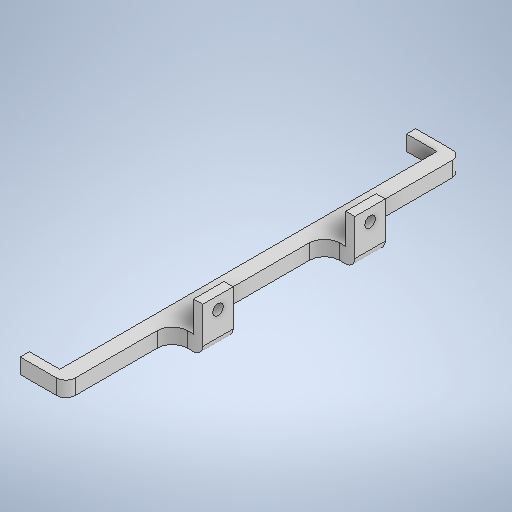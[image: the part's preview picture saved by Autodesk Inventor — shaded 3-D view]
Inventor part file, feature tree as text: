
AUTODESK INVENTOR PART (.ipt)
format: ipt  version: 2025 (Build 290162000, 162)  size: 331,776 bytes
history: native  units: mm
features: extrude x5, sketch x5, fillet x3
ambient origin geometry x8: Origin, YZ Plane, XZ Plane, XY Plane, X Axis, Y Axis, Z Axis, Center Point
bodies: Solide1 (feature_tree)
feature tree (13):
  extrude  "Extrusion1"  Depth=130.0mm
  extrude  "Extrusion2"  Depth=5.0mm
  extrude  "Extrusion3"  Depth=5.0mm TaperAngle=0.0deg
  extrude  "Extrusion4"  Depth=10.0mm
  fillet  "Congé1"  Radius=20.0mm
  fillet  "Congé2"  Radius=10.0mm
  fillet  "Congé3"  Radius=10.0mm
  extrude  "Extrusion5"  Depth=3.5mm
  sketch  "Esquisse1"
  sketch  "Esquisse2"
  sketch  "Esquisse3"
  sketch  "Esquisse4"
  sketch  "Esquisse5"
